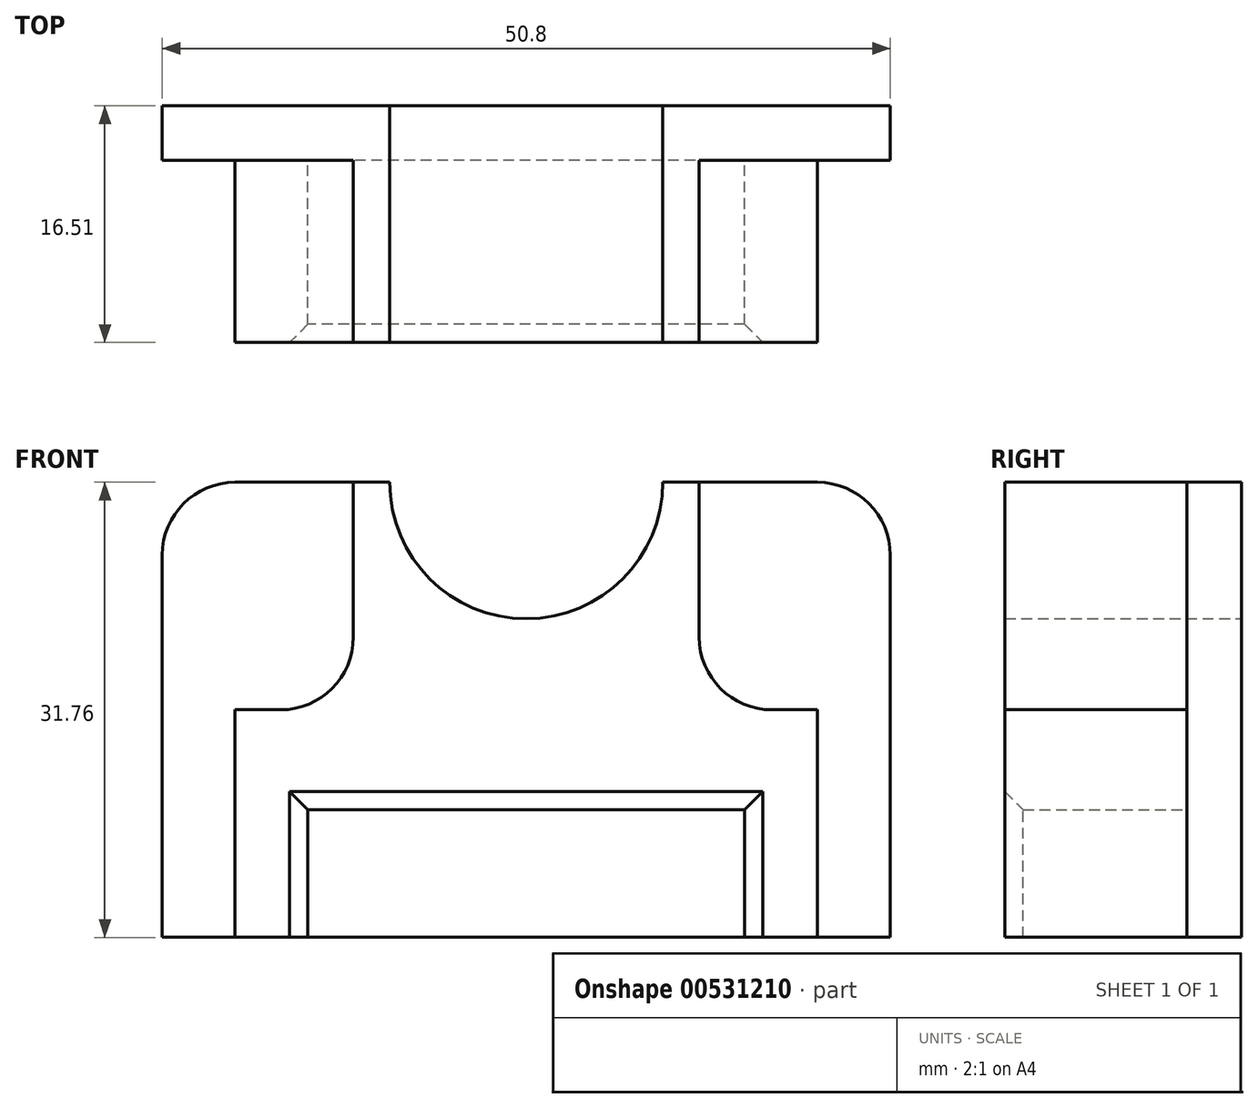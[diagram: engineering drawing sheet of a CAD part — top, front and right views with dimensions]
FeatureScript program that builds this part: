
annotation { "Feature Type Name" : "Feature", "Feature Type Description" : "" }
export const myFeature = defineFeature(function(context is Context, id is Id, definition is map)
    precondition{}
    {
        {
            var Q0;
            Q0=qCreatedBy(makeId("Front.planeOp"),FACE);
            var sketch = newSketch(context, id + "F0", { "sketchPlane" : qUnion([Q0])});
            skLineSegment(sketch, "E0.bottom", {"start": v(20.32, 15.88) * mm, "end": v(9.53, 15.88) * mm});
            skLineSegment(sketch, "E0.top", {"start": v(25.4, -15.88) * mm, "end": v(-25.4, -15.88) * mm});
            skLineSegment(sketch, "E0.left", {"start": v(25.4, 10.8) * mm, "end": v(25.4, -15.88) * mm});
            skLineSegment(sketch, "E0.right", {"start": v(-25.4, 10.8) * mm, "end": v(-25.4, -15.88) * mm});
            skPoint(sketch, "E0.middle", {"position": v(0, 0) * mm});
            skArc(sketch, "E1", {"start": v(-9.52, 15.88) * mm, "mid": v(0, 6.35) * mm, "end": v(9.53, 15.88) * mm});
            skLineSegment(sketch, "E2.trimOffspring", {"start": v(-9.52, 15.88) * mm, "end": v(-20.32, 15.88) * mm});
            skPoint(sketch, "E3.visualSharp", {"position": v(-25.4, 15.88) * mm});
            skArc(sketch, "E3.filletArc", {"start": v(-20.32, 15.88) * mm, "mid": v(-23.91, 14.39) * mm, "end": v(-25.4, 10.8) * mm});
            skPoint(sketch, "E4.visualSharp", {"position": v(25.4, 15.88) * mm});
            skArc(sketch, "E4.filletArc", {"start": v(25.4, 10.8) * mm, "mid": v(23.91, 14.39) * mm, "end": v(20.32, 15.88) * mm});
            skSolve(sketch);
        }
        {
            var Q0;
            Q0 = qSketchRegion(id + "F0", true);
            extrude(context, id + "F1", {"entities" : qUnion([Q0]), "depth" : 3.8 * mm, "offsetDistance" : 25.4 * mm});
        }
        {
            var Q0;
            Q0=makeQuery(id+"F1.opExtrude","CAP_FACE",FACE,{"disambiguationData":[OSD([sQuery(id+"F0.wireOp",EDGE,"E0.bottom"),sQuery(id+"F0.wireOp",EDGE,"E0.top"),sQuery(id+"F0.wireOp",EDGE,"E0.left"),sQuery(id+"F0.wireOp",EDGE,"E0.right"),sQuery(id+"F0.wireOp",EDGE,"E1"),sQuery(id+"F0.wireOp",EDGE,"E2.trimOffspring"),sQuery(id+"F0.wireOp",EDGE,"E3.filletArc"),sQuery(id+"F0.wireOp",EDGE,"E4.filletArc")])],"isStart":false});
            var sketch = newSketch(context, id + "F2", { "sketchPlane" : qUnion([Q0])});
            skArc(sketch, "E5", {"start": v(-9.52, 15.88) * mm, "mid": v(0, 6.35) * mm, "end": v(9.53, 15.87) * mm});
            skLineSegment(sketch, "E6", {"start": v(9.53, 15.88) * mm, "end": v(12.07, 15.88) * mm});
            skLineSegment(sketch, "E7", {"start": v(12.07, 15.88) * mm, "end": v(12.07, 5.08) * mm});
            skLineSegment(sketch, "E8", {"start": v(17.15, 0) * mm, "end": v(20.32, 0) * mm});
            skLineSegment(sketch, "E9", {"start": v(20.32, 0) * mm, "end": v(20.32, -15.88) * mm});
            skLineSegment(sketch, "E10", {"start": v(20.32, -15.88) * mm, "end": v(15.24, -15.88) * mm});
            skLineSegment(sketch, "E11", {"start": v(15.24, -15.88) * mm, "end": v(15.24, -6.99) * mm});
            skLineSegment(sketch, "E12", {"start": v(15.24, -6.99) * mm, "end": v(0, -6.99) * mm});
            skLineSegment(sketch, "E13", {"start": v(0, -6.99) * mm, "end": v(0, 6.35) * mm, "construction": true});
            skLineSegment(sketch, "E14.MirrorCS", {"start": v(-9.52, 15.88) * mm, "end": v(-12.06, 15.88) * mm});
            skLineSegment(sketch, "E15.MirrorCS", {"start": v(-12.06, 15.88) * mm, "end": v(-12.06, 5.08) * mm});
            skLineSegment(sketch, "E16.MirrorCS", {"start": v(-15.24, -6.98) * mm, "end": v(0, -6.99) * mm});
            skLineSegment(sketch, "E17.MirrorCS", {"start": v(-15.24, -15.88) * mm, "end": v(-15.24, -6.99) * mm});
            skLineSegment(sketch, "E18.MirrorCS", {"start": v(-20.32, -15.87) * mm, "end": v(-15.24, -15.87) * mm});
            skLineSegment(sketch, "E19.MirrorCS", {"start": v(-20.32, 0) * mm, "end": v(-20.32, -15.88) * mm});
            skLineSegment(sketch, "E20.MirrorCS", {"start": v(-17.15, 0) * mm, "end": v(-20.32, 0) * mm});
            skArc(sketch, "E21", {"start": v(9.53, 15.88) * mm, "mid": v(0, 6.35) * mm, "end": v(-9.52, 15.88) * mm});
            skPoint(sketch, "E22.visualSharp", {"position": v(12.07, 0) * mm});
            skArc(sketch, "E22.filletArc", {"start": v(12.07, 5.08) * mm, "mid": v(13.55, 1.49) * mm, "end": v(17.15, 0) * mm});
            skPoint(sketch, "E23.visualSharp", {"position": v(-12.07, 0) * mm});
            skArc(sketch, "E23.filletArc", {"start": v(-17.15, 0) * mm, "mid": v(-13.55, 1.49) * mm, "end": v(-12.07, 5.08) * mm});
            skSolve(sketch);
        }
        {
            var Q0;
            Q0 = qSketchRegion(id + "F2", true);
            extrude(context, id + "F3", {"entities" : qUnion([Q0]), "operationType" : NewBodyOperationType.ADD, "depth" : 12.7 * mm, "offsetDistance" : 25.4 * mm});
        }
        {
            var Q0;
            Q0=makeQuery(id+"F3.opExtrude","CAP_EDGE",EDGE,{"disambiguationData":[OSD([sQuery(id+"F2.wireOp",EDGE,"E21")])],"isStart":false});
            var Q1;
            Q1=makeQuery(id+"F3.opExtrude","CAP_EDGE",EDGE,{"disambiguationData":[OSD([sQuery(id+"F2.wireOp",EDGE,"E17.MirrorCS")])],"isStart":false});
            var Q2;
            Q2=makeQuery(id+"F3.opExtrude","CAP_EDGE",EDGE,{"disambiguationData":[OSD([sQuery(id+"F2.wireOp",EDGE,"E12"),sQuery(id+"F2.wireOp",EDGE,"E16.MirrorCS")])],"isStart":false});
            var Q3;
            Q3=makeQuery(id+"F3.opExtrude","CAP_EDGE",EDGE,{"disambiguationData":[OSD([sQuery(id+"F2.wireOp",EDGE,"E11")])],"isStart":false});
            chamfer(context, id + "F4", {"entities" : qUnion([Q0, Q1, Q2, Q3]), "width" : 1.27 * mm, "tangentPropagation" : true});
        }
    });
